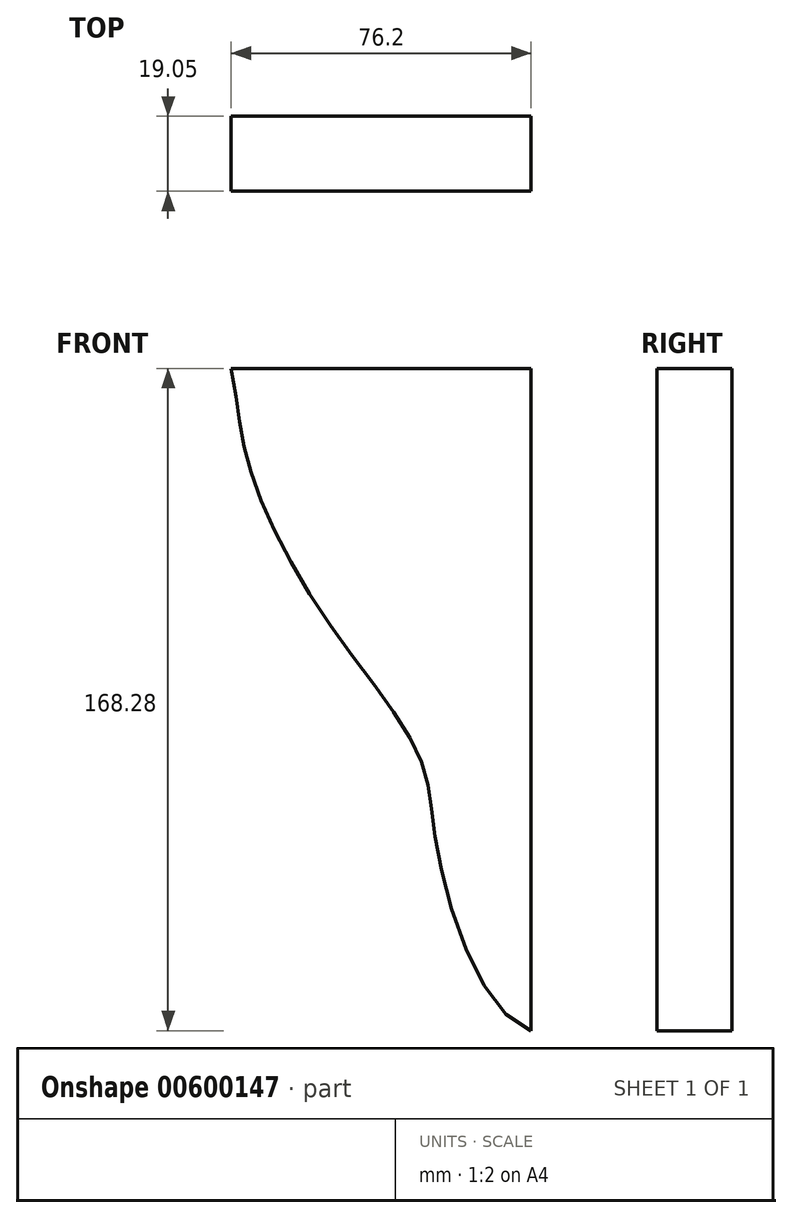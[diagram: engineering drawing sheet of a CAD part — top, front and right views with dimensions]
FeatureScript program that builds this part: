
annotation { "Feature Type Name" : "Feature", "Feature Type Description" : "" }
export const myFeature = defineFeature(function(context is Context, id is Id, definition is map)
    precondition{}
    {
        {
            var Q0;
            Q0=qCreatedBy(makeId("Front.planeOp"),FACE);
            var sketch = newSketch(context, id + "F0", { "sketchPlane" : qUnion([Q0])});
            skLineSegment(sketch, "E0.bottom", {"start": v(-55.46, 152.4) * mm, "end": v(20.74, 152.4) * mm});
            skLineSegment(sketch, "E0.right", {"start": v(20.74, 152.4) * mm, "end": v(20.74, -15.88) * mm});
            skFitSpline(sketch, "E1", {"points": [v(-55.46, 152.4) * mm, v(-50.8, 127) * mm, v(-31.01, 88.14) * mm, v(-7.65, 53.73) * mm, v(-2.82, 28.33) * mm, v(20.74, -15.88) * mm], "startDerivative": vector(32.58, -176) * mm, "endDerivative": vector(156.51, -51.12) * mm});
            skSolve(sketch);
        }
        {
            var Q0;
            Q0 = qSketchRegion(id + "F0", true);
            extrude(context, id + "F1", {"entities" : qUnion([Q0]), "depth" : 19.05 * mm, "offsetDistance" : 25.4 * mm});
        }
    });
